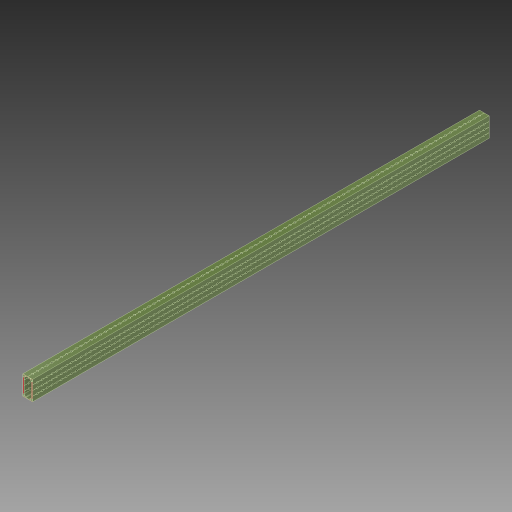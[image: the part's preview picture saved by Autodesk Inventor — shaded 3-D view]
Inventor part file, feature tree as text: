
AUTODESK INVENTOR PART (.ipt)
format: ipt  version: 2023.4 (Build 274418000, 418)  size: 6,216,192 bytes
history: native  units: in
note: dims shown in document units (in); Inventor stores cm internally (conversion verified against a paired STEP export)
features: extrude x1, sketch x1, other x1
ambient origin geometry x8: Origin, YZ Plane, XZ Plane, XY Plane, X Axis, Y Axis, Z Axis, Center Point
bodies: Solid1 (feature_tree)
feature tree (3):
  extrude  "CUT_LENGTH"  [1 undecoded]
  sketch  "Sketch1"  dims[d0=0.001in d1=0.0in]
  other  "REV-21-2590"
note: 1 required parameter value undecoded (feature->parameter linkage not recoverable at this tier; creation-order binding heuristic only, values carry confidence <= 0.55)
